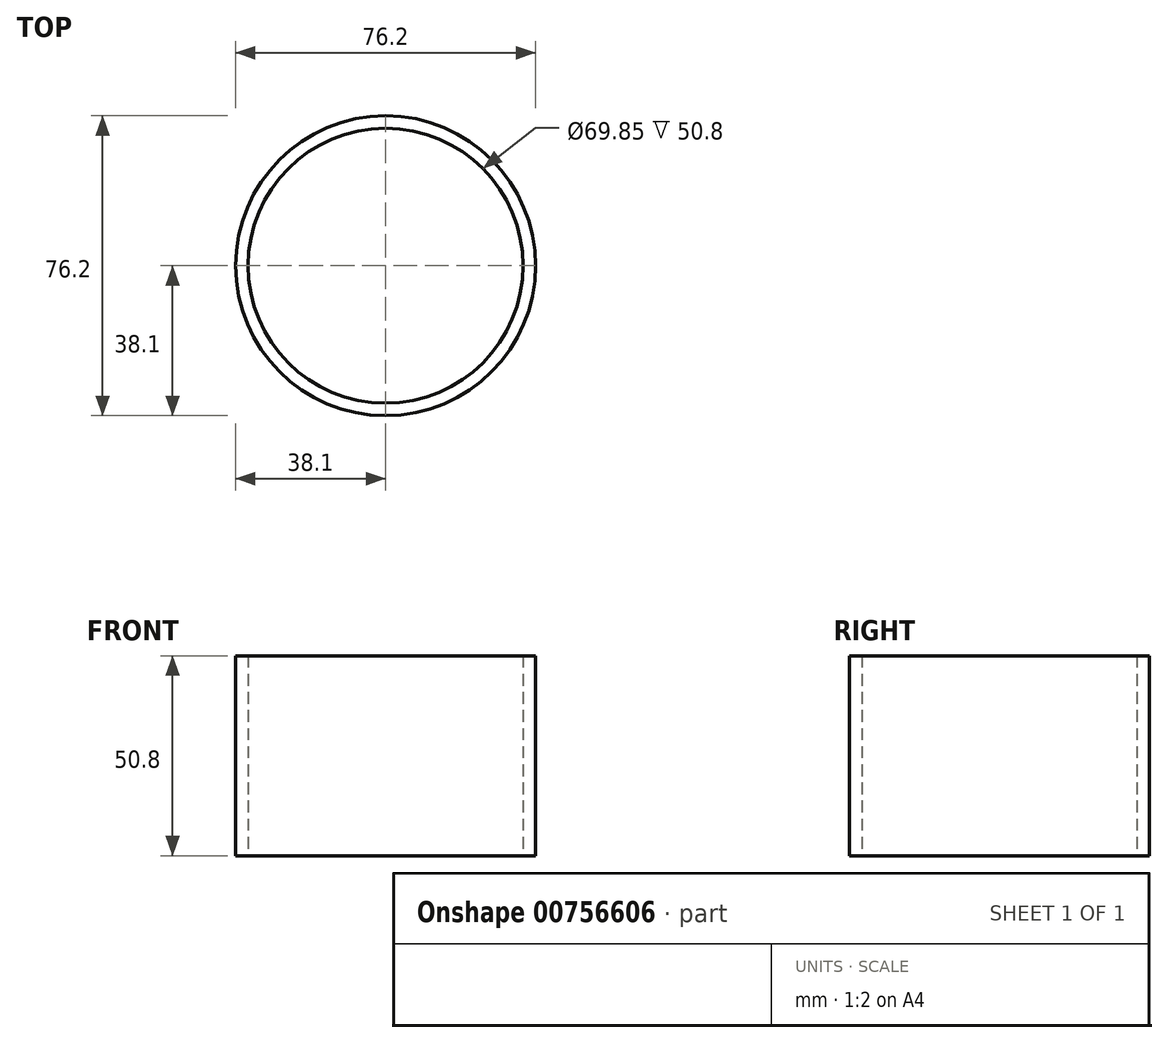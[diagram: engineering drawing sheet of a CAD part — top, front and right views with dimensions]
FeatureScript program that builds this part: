
annotation { "Feature Type Name" : "Feature", "Feature Type Description" : "" }
export const myFeature = defineFeature(function(context is Context, id is Id, definition is map)
    precondition{}
    {
        {
            var Q0;
            Q0=qCreatedBy(makeId("Top.planeOp"),FACE);
            var sketch = newSketch(context, id + "F0", { "sketchPlane" : qUnion([Q0])});
            skCircle(sketch, "E0", {"center": v(0, 0) * mm, "radius": 38.1 * mm});
            skCircle(sketch, "E1", {"center": v(0, 0) * mm, "radius": 34.93 * mm});
            skSolve(sketch);
        }
        {
            var Q0;
            Q0=makeQuery(id+"F0.imprint","IMPRINT",FACE,{"disambiguationData":[TD([[makeQuery(id+"F0.imprint","IMPRINT",EDGE,{"derivedFrom":sQuery(id+"F0.wireOp",EDGE,"E0")}),1.0]])]});
            extrude(context, id + "F1", {"entities" : qUnion([Q0]), "depth" : 50.8 * mm});
        }
    });
